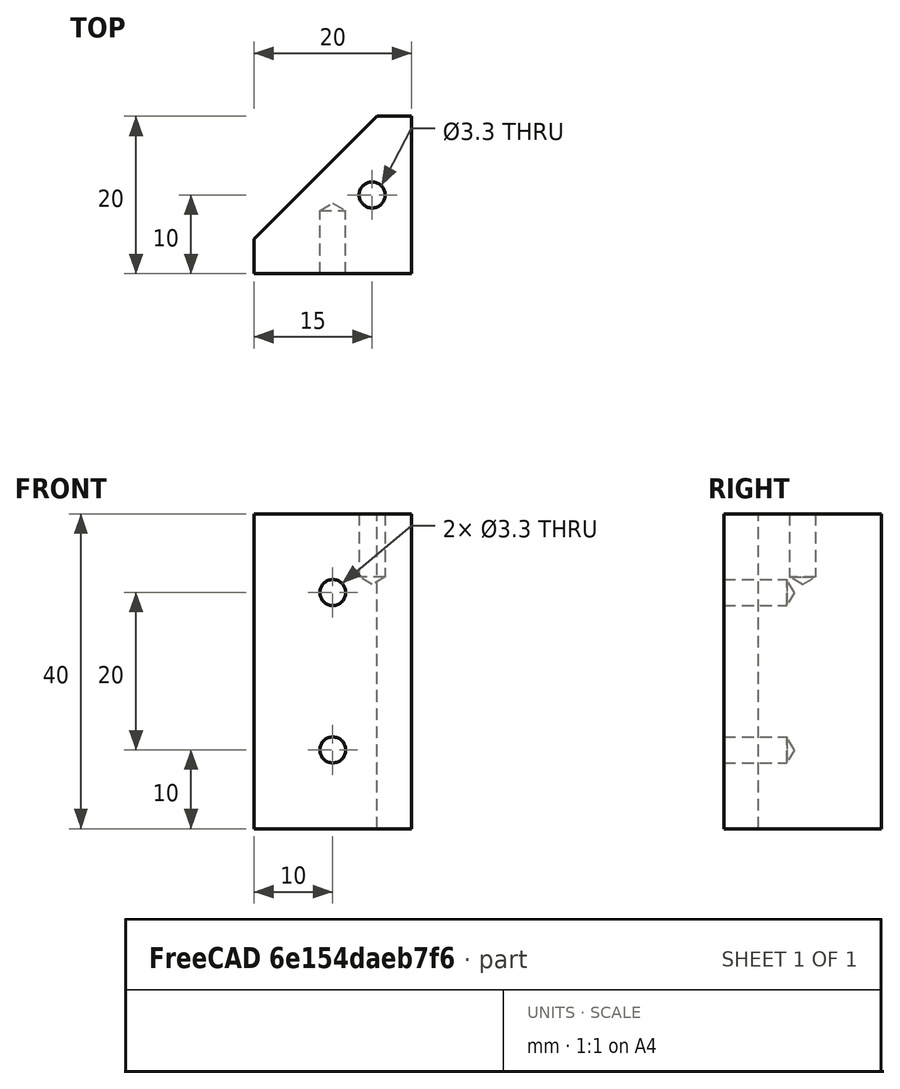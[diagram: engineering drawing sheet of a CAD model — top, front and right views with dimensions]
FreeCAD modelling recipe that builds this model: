
FCSTD DOCUMENT  (FreeCAD 1.0R39319 (Git))
Label: OCT-ULBLK-AA
License: Creative Commons Attribution 4.0
LicenseURL: https://creativecommons.org/licenses/by/4.0/
objects: TechDraw::DrawViewDimension×11, Sketcher::SketchObject×3, PartDesign::Hole×2, TechDraw::DrawProjGroupItem×2, PartDesign::Pad×1, PartDesign::Body×1, TechDraw::DrawSVGTemplate×1, TechDraw::DrawProjGroup×1, TechDraw::DrawPage×1
note: 32 computed .brp shape members not serialized (recipe doc carries the construction recipe); baked Part::Feature solids carry a one-line shape summary decoded from their .brp

FEATURE [Sketcher::SketchObject] Sketch
  ArcFitTolerance = 1e-06
  AttachmentSupport = -> [XY_Plane]
  FullyConstrained = true
  MakeInternals = false
  MapMode = 5
  sketch-geometry (5):
    g0: LineSegment StartX=-85 StartY=0 StartZ=0 EndX=-65 EndY=0 EndZ=0
    g1: LineSegment StartX=-65 StartY=0 StartZ=0 EndX=-65 EndY=20 EndZ=0
    g2: LineSegment StartX=-85 StartY=4.4 StartZ=0 EndX=-85 EndY=0 EndZ=0
    g3: LineSegment StartX=-65 StartY=20 StartZ=0 EndX=-69.4 EndY=20 EndZ=0
    g4: LineSegment StartX=-69.4 StartY=20 StartZ=0 EndX=-85 EndY=4.4 EndZ=0
  constraints (15):
    c: Coincident(g0,g1)
    c: Coincident(g2,g0)
    c: Horizontal(g0)
    c: Vertical(g1)
    c: Vertical(g2)
    c: PointOnObject(g0,g-1)
    c: DistanceY(g1,g1) = 20
    c: DistanceX(g0,g0) = 20
    c: DistanceX(g0,g-1) = 85
    c: Coincident(g1,g3)
    c: Horizontal(g3)
    c: Coincident(g3,g4)
    c: Coincident(g4,g2)
    c: DistanceY(g2,g2) = 4.4
    c: Angle(g2,g4) = 2.35619
FEATURE [PartDesign::Pad] Pad
  Direction = (0,0,1)
  Length = 40
  Length2 = 10
  Profile = -> Sketch
  ReferenceAxis = -> Sketch [N_Axis]
  Suppressed = false
  Type = 0
FEATURE [Sketcher::SketchObject] Sketch001
  ArcFitTolerance = 1e-06
  AttachmentSupport = -> [Pad]
  ExternalGeometry = -> [Pad]
  FullyConstrained = true
  MakeInternals = false
  MapMode = 5
  Placement = pos=(0,0,0) rot=(1,0,0;1.5708rad)
  sketch-geometry (3):
    g0: LineSegment [constr] StartX=-75 StartY=30 StartZ=0 EndX=-75 EndY=10 EndZ=0
    g1: Circle CenterX=-75 CenterY=30 CenterZ=0 NormalX=0 NormalY=0 NormalZ=1 AngleXU=0 Radius=2
    g2: Circle CenterX=-75 CenterY=10 CenterZ=0 NormalX=0 NormalY=0 NormalZ=1 AngleXU=0 Radius=2
  constraints (8):
    c: Vertical(g0)
    c: Coincident(g1,g0)
    c: Coincident(g2,g0)
    c: Equal(g1,g2)
    c: Diameter(g1) = 4
    c: DistanceX(g0,g-1) = 75
    c: DistanceY(g-1,g0) = 10
    c: DistanceY(g0,g0) = 20
FEATURE [PartDesign::Hole] Hole
  BaseFeature = -> Pad
  CustomThreadClearance = 0
  Depth = 8
  DepthType = 0
  Diameter = 3.3
  DrillForDepth = false
  DrillPoint = 1
  DrillPointAngle = 118
  HoleCutCountersinkAngle = 90
  HoleCutCustomValues = false
  HoleCutDepth = 0
  HoleCutDiameter = 6.1
  HoleCutType = 0
  ModelThread = false
  Profile = -> Sketch001
  Suppressed = false
  Tapered = false
  TaperedAngle = 90
  ThreadClass = 0
  ThreadDepth = 8
  ThreadDepthType = 0
  ThreadDirection = 0
  ThreadFit = 0
  ThreadSize = 11
  ThreadType = 1
  Threaded = true
  UseCustomThreadClearance = false
FEATURE [Sketcher::SketchObject] Sketch002
  ArcFitTolerance = 1e-06
  AttachmentSupport = -> [Hole]
  FullyConstrained = false
  MakeInternals = false
  MapMode = 5
  Placement = pos=(0,0,40) rot=(0,0,1;0rad)
  sketch-geometry (1):
    g0: Circle CenterX=-70 CenterY=10 CenterZ=0 NormalX=0 NormalY=0 NormalZ=1 AngleXU=0 Radius=1.81729
  constraints (2):
    c: Distance(g0,g-2) = 70
    c: Distance(g0,g-1) = 10
FEATURE [PartDesign::Hole] Hole001
  BaseFeature = -> Hole
  CustomThreadClearance = 0
  Depth = 8
  DepthType = 0
  Diameter = 3.3
  DrillForDepth = false
  DrillPoint = 1
  DrillPointAngle = 118
  HoleCutCountersinkAngle = 90
  HoleCutCustomValues = false
  HoleCutDepth = 0
  HoleCutDiameter = 6.1
  HoleCutType = 0
  ModelThread = false
  Profile = -> Sketch002
  Suppressed = false
  Tapered = false
  TaperedAngle = 90
  ThreadClass = 0
  ThreadDepth = 8
  ThreadDepthType = 0
  ThreadDirection = 0
  ThreadFit = 0
  ThreadSize = 11
  ThreadType = 1
  Threaded = true
  UseCustomThreadClearance = false
FEATURE [PartDesign::Body] Body  label="upper left block"
  AllowCompound = false
  Group = -> [Sketch,Pad,Sketch001,Hole,Sketch002,Hole001]
  Origin = -> Origin
  Tip = -> Hole001
FEATURE [TechDraw::DrawSVGTemplate] Template
  EditableTexts = approval_person=S. Aphelion; creator=Michael Stoll; date_of_issue=08/02/2026; document_status=In preparation; document_type=Component Drawing; drawing_number=DN; general_tolerances=ISO 2768-m; language_code=EN; part_material=Aluminium 6082 T6; responsible_department=RD; revision_index=A; scale=2 : 1; sheet_number=1 / 1; supplementary_title_1=Upper Left Panel Block; title=OCT-ULBLK-AA
  Height = 297
  Orientation = 1
  Template = C:/Program Files/FreeCAD 1.0/data/Mod/TechDraw/Templates/A3_Landscape_ISO5457_advanced.svg
  Width = 420
FEATURE [TechDraw::DrawProjGroupItem] View  label="Front"
  CoarseView = false
  Direction = (0,-1,0)
  Focus = 100
  HardHidden = false
  IsoCount = 0
  IsoHidden = false
  IsoVisible = false
  LockPosition = true
  Perspective = false
  Rotation = 0
  RotationVector = (1,0,0)
  Scale = 2
  ScaleType = 2
  ScrubCount = 1
  SeamHidden = false
  SeamVisible = false
  SmoothHidden = false
  SmoothVisible = true
  Source = -> [Body]
  Type = 0
  X = 0
  XDirection = (1,0,0)
  Y = 0
FEATURE [TechDraw::DrawProjGroupItem] ProjItem  label="Top"
  CoarseView = false
  Direction = (0,0,1)
  Focus = 100
  HardHidden = false
  IsoCount = 0
  IsoHidden = false
  IsoVisible = false
  LockPosition = false
  Perspective = false
  Rotation = 0
  RotationVector = (1,0,0)
  Scale = 2
  ScaleType = 0
  ScrubCount = 1
  SeamHidden = false
  SeamVisible = false
  SmoothHidden = false
  SmoothVisible = true
  Source = -> [Body]
  Type = 4
  X = 0
  XDirection = (1,0,0)
  Y = 110
FEATURE [TechDraw::DrawProjGroup] ProjGroup
  Anchor = -> View
  AutoDistribute = true
  LockPosition = false
  ProjectionType = 1
  Rotation = 0
  Scale = 2
  ScaleType = 0
  Source = -> [Body]
  Views = -> [View,ProjItem]
  X = 158.571
  Y = 100.408
  spacingX = 15
  spacingY = 50
FEATURE [TechDraw::DrawViewDimension] Dimension
  AngleOverride = false
  Arbitrary = false
  ArbitraryTolerances = false
  BoxCorners = (2) [(-20,-20,0),(20,20,0)]
  EqualTolerance = true
  ExtensionAngle = 0
  FormatSpec = %.1f
  FormatSpecOverTolerance = %+.1f
  FormatSpecUnderTolerance = %+.1f
  Inverted = false
  LineAngle = 0
  LockPosition = false
  MeasureType = 1
  OverTolerance = 0
  References2D = -> [ProjItem]
  Rotation = 0
  Scale = 2
  ScaleType = 0
  TheoreticalExact = false
  Type = 2
  UnderTolerance = 0
  X = 48.9856
  Y = 0
FEATURE [TechDraw::DrawViewDimension] Dimension001
  AngleOverride = false
  Arbitrary = false
  ArbitraryTolerances = false
  BoxCorners = (2) [(-20,-40,0),(20,40,0)]
  EqualTolerance = true
  ExtensionAngle = 0
  FormatSpec = %.1f
  FormatSpecOverTolerance = %+.1f
  FormatSpecUnderTolerance = %+.1f
  Inverted = false
  LineAngle = 0
  LockPosition = false
  MeasureType = 1
  OverTolerance = 0
  References2D = -> [View]
  Rotation = 0
  Scale = 2
  ScaleType = 0
  TheoreticalExact = false
  Type = 2
  UnderTolerance = 0
  X = 35.4487
  Y = 0
FEATURE [TechDraw::DrawViewDimension] Dimension002
  AngleOverride = false
  Arbitrary = false
  ArbitraryTolerances = false
  BoxCorners = (2) [(-20,-40,0),(20,40,0)]
  EqualTolerance = true
  ExtensionAngle = 0
  FormatSpec = %.1f
  FormatSpecOverTolerance = %+.1f
  FormatSpecUnderTolerance = %+.1f
  Inverted = false
  LineAngle = 0
  LockPosition = false
  MeasureType = 1
  OverTolerance = 0
  References2D = -> [View]
  Rotation = 0
  Scale = 2
  ScaleType = 0
  TheoreticalExact = false
  Type = 1
  UnderTolerance = 0
  X = 0
  Y = -59.7687
FEATURE [TechDraw::DrawViewDimension] Dimension003
  AngleOverride = false
  Arbitrary = false
  ArbitraryTolerances = false
  BoxCorners = (2) [(-20,-40,0),(20,40,0)]
  EqualTolerance = true
  ExtensionAngle = 0
  FormatSpec = ⌀%.1f
  FormatSpecOverTolerance = %+.1f
  FormatSpecUnderTolerance = %+.1f
  Inverted = false
  LineAngle = 0
  LockPosition = false
  MeasureType = 1
  OverTolerance = 0
  References2D = -> [View]
  Rotation = 0
  Scale = 2
  ScaleType = 0
  TheoreticalExact = false
  Type = 5
  UnderTolerance = 0
  X = -39.4185
  Y = 55.0742
FEATURE [TechDraw::DrawViewDimension] Dimension004
  AngleOverride = false
  Arbitrary = false
  ArbitraryTolerances = false
  BoxCorners = (2) [(-20,-40,0),(20,40,0)]
  EqualTolerance = true
  ExtensionAngle = 0
  FormatSpec = %.1f
  FormatSpecOverTolerance = %+.1f
  FormatSpecUnderTolerance = %+.1f
  Inverted = false
  LineAngle = 0
  LockPosition = false
  MeasureType = 1
  OverTolerance = 0
  References2D = -> [View]
  Rotation = 0
  Scale = 2
  ScaleType = 0
  TheoreticalExact = false
  Type = 0
  UnderTolerance = 0
  X = -41.2821
  Y = -30
FEATURE [TechDraw::DrawViewDimension] Dimension005
  AngleOverride = false
  Arbitrary = false
  ArbitraryTolerances = false
  BoxCorners = (2) [(-20,-40,0),(20,40,0)]
  EqualTolerance = true
  ExtensionAngle = 0
  FormatSpec = %.1f
  FormatSpecOverTolerance = %+.1f
  FormatSpecUnderTolerance = %+.1f
  Inverted = false
  LineAngle = 0
  LockPosition = false
  MeasureType = 1
  OverTolerance = 0
  References2D = -> [View]
  Rotation = 0
  Scale = 2
  ScaleType = 0
  TheoreticalExact = false
  Type = 2
  UnderTolerance = 0
  X = -41.2821
  Y = 0
FEATURE [TechDraw::DrawViewDimension] Dimension006
  AngleOverride = false
  Arbitrary = false
  ArbitraryTolerances = false
  BoxCorners = (2) [(-20,-20,0),(20,20,0)]
  EqualTolerance = true
  ExtensionAngle = 0
  FormatSpec = %.1f
  FormatSpecOverTolerance = %+.1f
  FormatSpecUnderTolerance = %+.1f
  Inverted = false
  LineAngle = 0
  LockPosition = false
  MeasureType = 1
  OverTolerance = 0
  References2D = -> [ProjItem]
  Rotation = 0
  Scale = 2
  ScaleType = 0
  TheoreticalExact = false
  Type = 0
  UnderTolerance = 0
  X = 31.7729
  Y = -10
FEATURE [TechDraw::DrawViewDimension] Dimension007
  AngleOverride = false
  Arbitrary = false
  ArbitraryTolerances = false
  BoxCorners = (2) [(-20,-20,0),(20,20,0)]
  EqualTolerance = true
  ExtensionAngle = 0
  FormatSpec = %.1f
  FormatSpecOverTolerance = %+.1f
  FormatSpecUnderTolerance = %+.1f
  Inverted = false
  LineAngle = 0
  LockPosition = false
  MeasureType = 1
  OverTolerance = 0
  References2D = -> [ProjItem]
  Rotation = 0
  Scale = 2
  ScaleType = 0
  TheoreticalExact = false
  Type = 0
  UnderTolerance = 0
  X = 15
  Y = 51.0719
FEATURE [TechDraw::DrawViewDimension] Dimension008
  AngleOverride = false
  Arbitrary = false
  ArbitraryTolerances = false
  BoxCorners = (2) [(-20,-20,0),(20,20,0)]
  EqualTolerance = true
  ExtensionAngle = 0
  FormatSpec = %.1f
  FormatSpecOverTolerance = %+.1f
  FormatSpecUnderTolerance = %+.1f
  Inverted = false
  LineAngle = 0
  LockPosition = false
  MeasureType = 1
  OverTolerance = 0
  References2D = -> [ProjItem]
  Rotation = 0
  Scale = 2
  ScaleType = 0
  TheoreticalExact = false
  Type = 2
  UnderTolerance = 0
  X = -49.5756
  Y = -15.6
FEATURE [TechDraw::DrawViewDimension] Dimension009
  AngleOverride = false
  Arbitrary = false
  ArbitraryTolerances = false
  BoxCorners = (2) [(-20,-20,0),(20,20,0)]
  EqualTolerance = true
  ExtensionAngle = 0
  FormatSpec = %.1f
  FormatSpecOverTolerance = %+.1f
  FormatSpecUnderTolerance = %+.1f
  Inverted = false
  LineAngle = 0
  LockPosition = false
  MeasureType = 1
  OverTolerance = 0
  References2D = -> [ProjItem]
  Rotation = 0
  Scale = 2
  ScaleType = 0
  TheoreticalExact = false
  Type = 6
  UnderTolerance = 0
  X = 75.5761
  Y = 23.7029
FEATURE [TechDraw::DrawViewDimension] Dimension010
  AngleOverride = false
  Arbitrary = false
  ArbitraryTolerances = false
  BoxCorners = (2) [(-20,-20,0),(20,20,0)]
  EqualTolerance = true
  ExtensionAngle = 0
  FormatSpec = ⌀%.1f
  FormatSpecOverTolerance = %+.1f
  FormatSpecUnderTolerance = %+.1f
  Inverted = false
  LineAngle = 0
  LockPosition = false
  MeasureType = 1
  OverTolerance = 0
  References2D = -> [ProjItem]
  Rotation = 0
  Scale = 2
  ScaleType = 0
  TheoreticalExact = false
  Type = 5
  UnderTolerance = 0
  X = -22.7724
  Y = 47.7528
FEATURE [TechDraw::DrawPage] Page
  KeepUpdated = true
  NextBalloonIndex = 1
  ProjectionType = 1
  Scale = 2
  Template = -> Template
  Views = -> [ProjGroup,Dimension,Dimension001,Dimension002,Dimension003,Dimension004,Dimension005,Dimension006,Dimension007,Dimension008,Dimension009,Dimension010]
